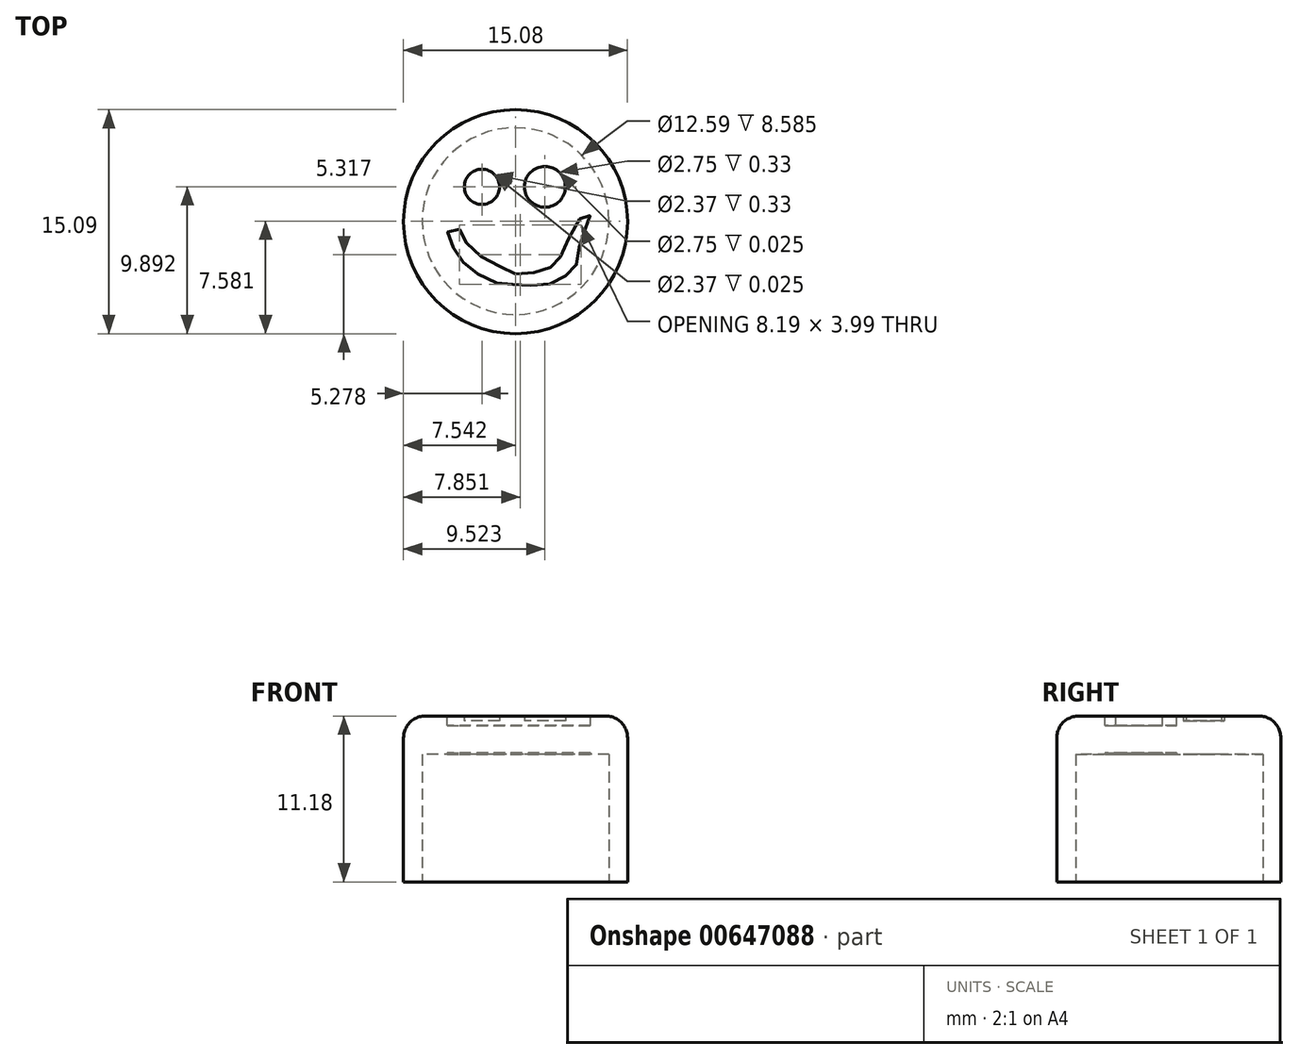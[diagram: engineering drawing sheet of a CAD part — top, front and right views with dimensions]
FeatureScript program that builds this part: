
annotation { "Feature Type Name" : "Feature", "Feature Type Description" : "" }
export const myFeature = defineFeature(function(context is Context, id is Id, definition is map)
    precondition{}
    {
        {
            var Q0;
            Q0=qCreatedBy(makeId("Top.planeOp"),FACE);
            var sketch = newSketch(context, id + "F0", { "sketchPlane" : qUnion([Q0])});
            skCircle(sketch, "E0", {"center": v(-5.64, -4.32) * mm, "radius": 6.3 * mm});
            skSolve(sketch);
        }
        {
            var Q0;
            Q0=qCreatedBy(makeId("Top.planeOp"),FACE);
            var sketch = newSketch(context, id + "F1", { "sketchPlane" : qUnion([Q0])});
            skCircle(sketch, "E1", {"center": v(-5.64, -4.35) * mm, "radius": 7.54 * mm});
            skSolve(sketch);
        }
        {
            var Q0;
            Q0=makeQuery(id+"F1.imprint","IMPRINT",FACE,{"disambiguationData":[TD([[makeQuery(id+"F1.imprint","IMPRINT",EDGE,{"derivedFrom":sQuery(id+"F1.wireOp",EDGE,"E1")}),1.0]])]});
            var Q1;
            Q1=sQuery(id+"F1.wireOp",EDGE,"E1");
            extrude(context, id + "F2", {"entities" : qUnion([Q0]), "surfaceEntities" : qUnion([Q1]), "depth" : 11.18 * mm, "offsetDistance" : 25.4 * mm});
        }
        {
            var Q0;
            Q0=makeQuery(id+"F0.imprint","IMPRINT",FACE,{"disambiguationData":[TD([[makeQuery(id+"F0.imprint","IMPRINT",EDGE,{"derivedFrom":sQuery(id+"F0.wireOp",EDGE,"E0")}),1.0]])]});
            var Q1;
            Q1=sQuery(id+"F0.wireOp",EDGE,"E0");
            extrude(context, id + "F3", {"entities" : qUnion([Q0]), "operationType" : NewBodyOperationType.REMOVE, "surfaceEntities" : qUnion([Q1]), "depth" : 8.6 * mm, "offsetDistance" : 25.4 * mm});
        }
        {
            var Q0;
            Q0=makeQuery(id+"F2.opExtrude","CAP_EDGE",EDGE,{"disambiguationData":[OSD([sQuery(id+"F1.wireOp",EDGE,"E1")])],"isStart":false});
            fillet(context, id + "F4", {"entities" : qUnion([Q0]), "radius" : 1.47 * mm, "tangentPropagation" : true, "allowEdgeOverflow" : false});
        }
        {
            var Q0;
            Q0=qCreatedBy(makeId("Top.planeOp"),FACE);
            var sketch = newSketch(context, id + "F5", { "sketchPlane" : qUnion([Q0])});
            skCircle(sketch, "E2", {"center": v(-7.9, -2) * mm, "radius": 1.18 * mm});
            skCircle(sketch, "E3", {"center": v(-3.66, -2) * mm, "radius": 1.38 * mm});
            skSolve(sketch);
        }
        {
            var Q0;
            Q0=makeQuery(id+"F5.imprint","IMPRINT",FACE,{"disambiguationData":[TD([[makeQuery(id+"F5.imprint","IMPRINT",EDGE,{"derivedFrom":sQuery(id+"F5.wireOp",EDGE,"E2")}),1.0]])]});
            var Q1;
            Q1=makeQuery(id+"F5.imprint","IMPRINT",FACE,{"disambiguationData":[TD([[makeQuery(id+"F5.imprint","IMPRINT",EDGE,{"derivedFrom":sQuery(id+"F5.wireOp",EDGE,"E3")}),1.0]])]});
            var Q2;
            Q2=sQuery(id+"F5.wireOp",EDGE,"E2");
            var Q3;
            Q3=sQuery(id+"F5.wireOp",EDGE,"E3");
            extrude(context, id + "F6", {"entities" : qUnion([Q0, Q1]), "operationType" : NewBodyOperationType.REMOVE, "surfaceEntities" : qUnion([Q2, Q3]), "depth" : 18.92 * mm, "offsetDistance" : 25.4 * mm});
        }
        {
            var Q0;
            Q0=qCreatedBy(makeId("Top.planeOp"),FACE);
            var sketch = newSketch(context, id + "F7", { "sketchPlane" : qUnion([Q0])});
            skFitSpline(sketch, "E4", {"points": [v(-9.43, -4.86) * mm, v(-8.82, -6.02) * mm, v(-6.91, -7.23) * mm, v(-5.51, -7.9) * mm, v(-3.76, -7.6) * mm, v(-2.84, -7.1) * mm, v(-2, -5.37) * mm, v(-0.91, -3.84) * mm, v(-0.6, -4.05) * mm, v(-1.2, -5.35) * mm, v(-1.47, -7.09) * mm, v(-2.27, -8.02) * mm, v(-3.77, -8.63) * mm, v(-5.6, -8.58) * mm, v(-6.9, -8.48) * mm, v(-8.77, -7.46) * mm, v(-9.72, -6.31) * mm, v(-10.18, -5) * mm, v(-9.43, -4.86) * mm]});
            skSolve(sketch);
        }
        {
            var Q0;
            Q0=makeQuery(id+"F7.imprint","IMPRINT",FACE,{"disambiguationData":[TD([[makeQuery(id+"F7.imprint","IMPRINT",EDGE,{"derivedFrom":sQuery(id+"F7.wireOp",EDGE,"E4")}),-1.0]])]});
            var Q1;
            Q1=sQuery(id+"F7.wireOp",EDGE,"E4");
            extrude(context, id + "F8", {"entities" : qUnion([Q0]), "operationType" : NewBodyOperationType.REMOVE, "surfaceEntities" : qUnion([Q1]), "depth" : 21.08 * mm, "offsetDistance" : 25.4 * mm});
        }
        {
            var Q0;
            Q0 = qSketchRegion(id + "F5", true);
            extrude(context, id + "F9", {"entities" : qUnion([Q0]), "operationType" : NewBodyOperationType.ADD, "depth" : 10.85 * mm, "offsetDistance" : 25.4 * mm});
        }
        {
            var Q0;
            Q0 = qSketchRegion(id + "F7", true);
            extrude(context, id + "F10", {"entities" : qUnion([Q0]), "operationType" : NewBodyOperationType.ADD, "depth" : 10.54 * mm, "offsetDistance" : 25.4 * mm});
        }
        {
            var Q0;
            Q0 = qSketchRegion(id + "F7", true);
            extrude(context, id + "F11", {"entities" : qUnion([Q0]), "operationType" : NewBodyOperationType.REMOVE, "depth" : 8.7 * mm, "offsetDistance" : 25.4 * mm});
        }
        {
            var Q0;
            Q0 = qSketchRegion(id + "F5", true);
            extrude(context, id + "F12", {"entities" : qUnion([Q0]), "operationType" : NewBodyOperationType.REMOVE, "depth" : 8.6 * mm, "offsetDistance" : 25.4 * mm});
        }
    });
